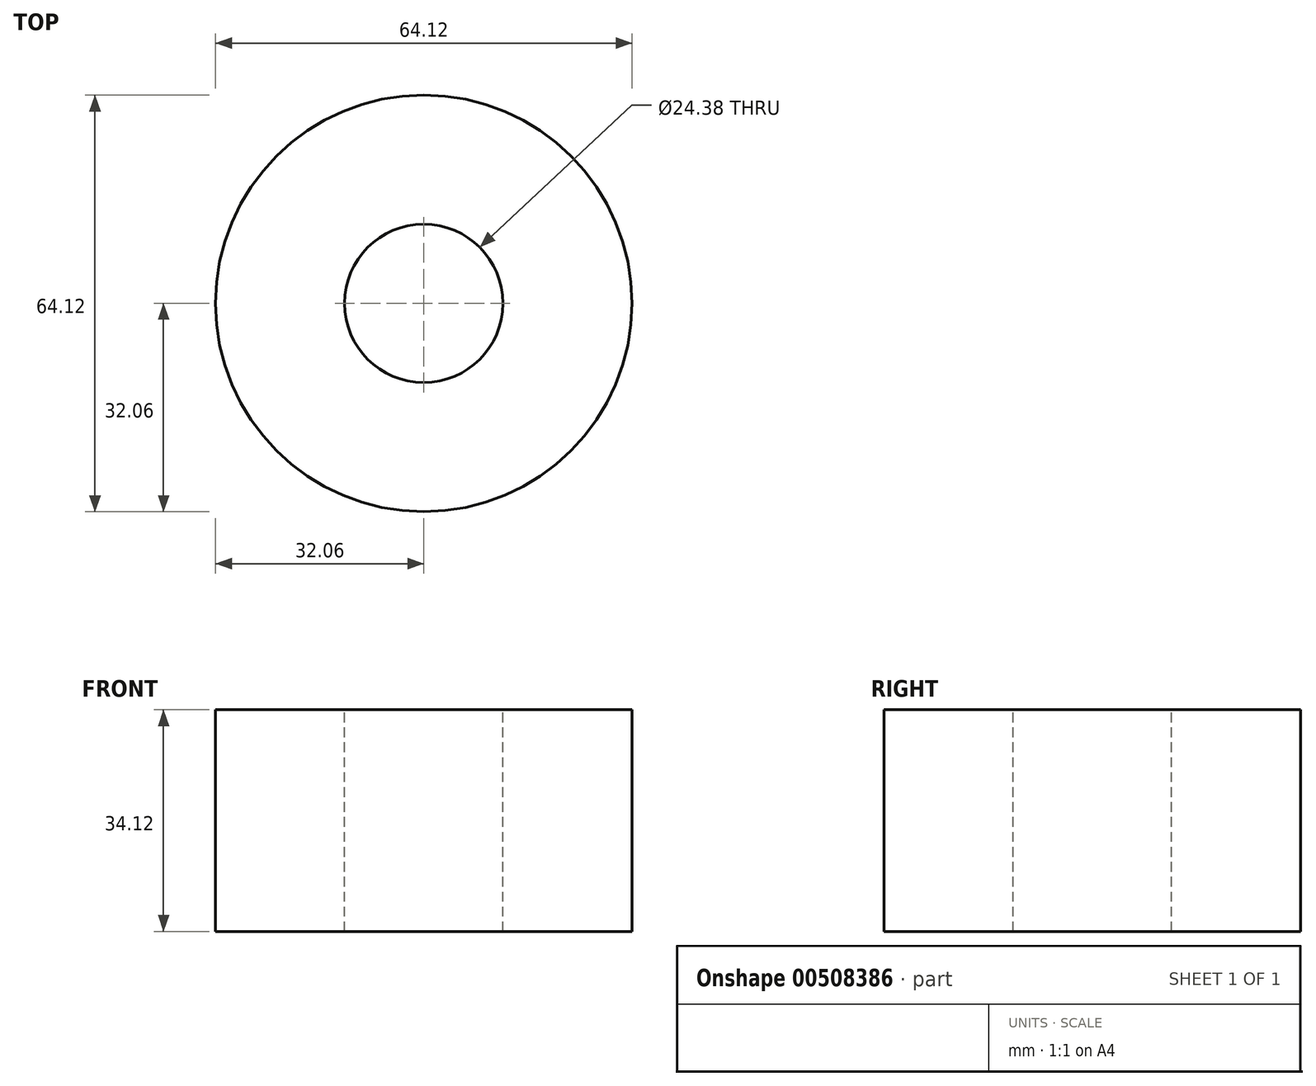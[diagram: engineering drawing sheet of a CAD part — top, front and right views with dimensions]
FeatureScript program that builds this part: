
annotation { "Feature Type Name" : "Feature", "Feature Type Description" : "" }
export const myFeature = defineFeature(function(context is Context, id is Id, definition is map)
    precondition{}
    {
        {
            var Q0;
            Q0=qCreatedBy(makeId("Front.planeOp"),FACE);
            var sketch = newSketch(context, id + "F0", { "sketchPlane" : qUnion([Q0])});
            skLineSegment(sketch, "E0", {"start": v(-40.04, 21.68) * mm, "end": v(-40.04, -42.38) * mm});
            skLineSegment(sketch, "E1", {"start": v(-40.04, -42.38) * mm, "end": v(49.96, -42.38) * mm});
            skLineSegment(sketch, "E2", {"start": v(49.96, -42.38) * mm, "end": v(49.96, -22.38) * mm});
            skLineSegment(sketch, "E3", {"start": v(49.96, -22.38) * mm, "end": v(-19.23, -22.38) * mm});
            skLineSegment(sketch, "E4", {"start": v(-19.23, -22.38) * mm, "end": v(-19.23, 22.76) * mm});
            skLineSegment(sketch, "E5.bottom", {"start": v(-64.13, -7.88) * mm, "end": v(-48.75, -7.88) * mm});
            skLineSegment(sketch, "E5.top", {"start": v(-64.13, -42.38) * mm, "end": v(-48.75, -42.38) * mm});
            skLineSegment(sketch, "E5.left", {"start": v(-64.13, -7.88) * mm, "end": v(-64.13, -42.38) * mm});
            skLineSegment(sketch, "E5.right", {"start": v(-48.75, -7.88) * mm, "end": v(-48.75, -42.38) * mm});
            skLineSegment(sketch, "E6", {"start": v(10.69, 60.38) * mm, "end": v(32.63, 30.94) * mm});
            skLineSegment(sketch, "E7", {"start": v(32.63, 30.94) * mm, "end": v(58.13, 43.69) * mm});
            skLineSegment(sketch, "E8.bottom", {"start": v(12.19, 22.31) * mm, "end": v(32.06, 22.31) * mm});
            skLineSegment(sketch, "E8.top", {"start": v(12.19, -11.81) * mm, "end": v(32.06, -11.81) * mm});
            skLineSegment(sketch, "E8.left", {"start": v(12.19, 22.31) * mm, "end": v(12.19, -11.81) * mm});
            skLineSegment(sketch, "E8.right", {"start": v(32.06, 22.31) * mm, "end": v(32.06, -11.81) * mm});
            skLineSegment(sketch, "E9.bottom", {"start": v(0, 34.5) * mm, "end": v(0, 34.5) * mm});
            skLineSegment(sketch, "E9.top", {"start": v(0, -30.19) * mm, "end": v(0, -30.19) * mm});
            skLineSegment(sketch, "E9.left", {"start": v(0, 34.5) * mm, "end": v(0, -30.19) * mm, "construction": true});
            skLineSegment(sketch, "E9.right", {"start": v(0, 34.5) * mm, "end": v(0, -30.19) * mm, "construction": true});
            skSolve(sketch);
        }
        {
            var Q0;
            Q0=makeQuery(id+"F0.imprint","IMPRINT",FACE,{"disambiguationData":[TD([[makeQuery(id+"F0.imprint","IMPRINT",EDGE,{"derivedFrom":sQuery(id+"F0.wireOp",EDGE,"E8.bottom")}),-1.0]])]});
            var Q1;
            Q1=sQuery(id+"F0.wireOp",EDGE,"E9.left");
            revolve(context, id + "F1", {"entities" : qUnion([Q0]), "axis" : qUnion([Q1]), "revolveType" : RevolveType.FULL});
        }
    });
